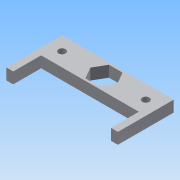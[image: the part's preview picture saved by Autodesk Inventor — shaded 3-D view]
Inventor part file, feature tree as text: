
AUTODESK INVENTOR PART (.ipt)
format: ipt  version: 2015 (Build 190159000, 159)  size: 141,312 bytes
history: native  units: mm
features: extrude x4, sketch x3, reference x2, projected_geometry x1
ambient origin geometry x8: Origin, YZ Plane, XZ Plane, XY Plane, X Axis, Y Axis, Z Axis, Center Point
bodies: Solid1 (feature_tree)
feature tree (10):
  extrude  "Extrusion1"  Depth=20.0mm
  extrude  "Extrusion2"  Depth=10.0mm TaperAngle=0.0deg
  extrude  "Extrusion3"  Depth=8.0mm
  extrude  "Extrusion7"  Depth=10.0mm TaperAngle=0.0deg
  sketch  "Sketch3"  dims[d0=80.0mm d1=20.0mm]
  sketch  "Sketch9"  dims[d2=8.0mm d3=0.0mm d13=10.0mm d14=0.0mm]
  reference  "Reference1"
  reference  "Reference2"
  sketch  "Sketch14"  dims[d40=5.2mm d41=60.0mm d42=10.0mm d43=0.0mm d65=19.5mm d70=40.0mm d73=10.0mm d74=5.0mm d75=20.0mm d76=8.0mm d77=0.0mm]
  projected_geometry  "Projected Loop2"
